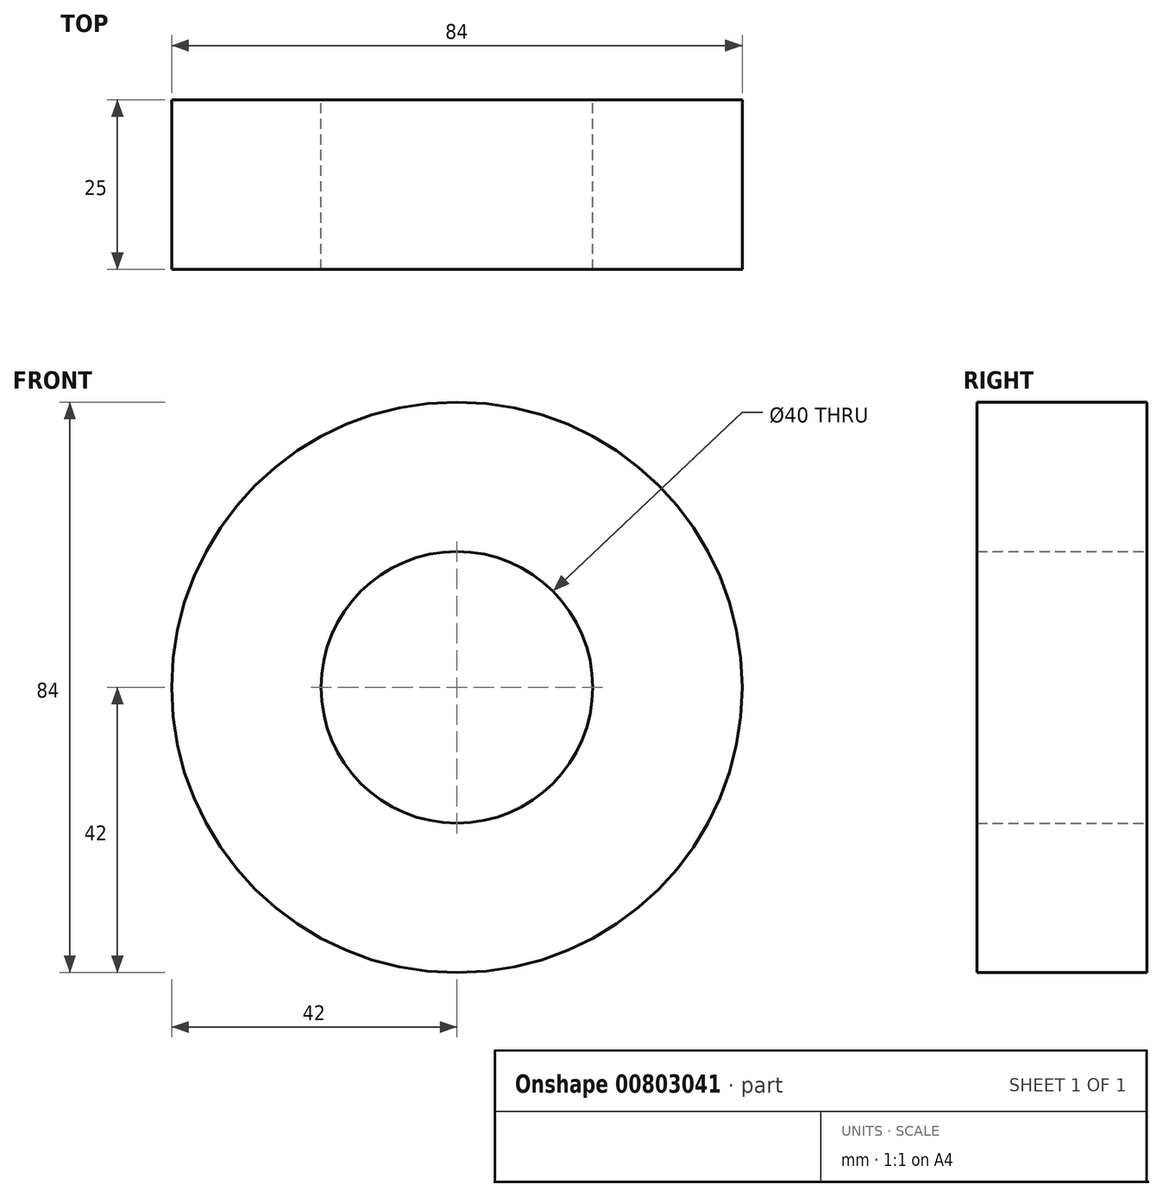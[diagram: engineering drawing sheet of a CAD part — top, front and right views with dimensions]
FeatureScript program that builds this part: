
annotation { "Feature Type Name" : "Feature", "Feature Type Description" : "" }
export const myFeature = defineFeature(function(context is Context, id is Id, definition is map)
    precondition{}
    {
        {
            var Q0;
            Q0=qCreatedBy(makeId("Front.planeOp"),FACE);
            var sketch = newSketch(context, id + "F0", { "sketchPlane" : qUnion([Q0])});
            skCircle(sketch, "E0", {"center": v(0, 0) * mm, "radius": 42 * mm});
            skCircle(sketch, "E1", {"center": v(0, 0) * mm, "radius": 20 * mm});
            skSolve(sketch);
        }
        {
            var Q0;
            Q0 = qSketchRegion(id + "F0", true);
            extrude(context, id + "F1", {"entities" : qUnion([Q0]), "depth" : 25 * mm, "offsetDistance" : 25 * mm});
        }
    });
